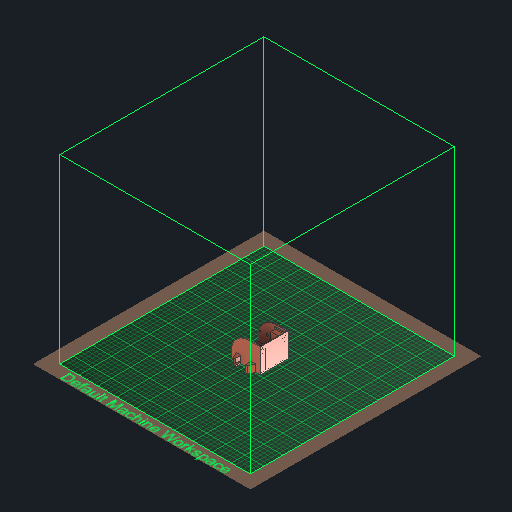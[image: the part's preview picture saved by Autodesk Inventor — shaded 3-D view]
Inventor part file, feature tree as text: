
AUTODESK INVENTOR PART (.ipt)
format: ipt  version: 2022 (Build 260153000, 153)  size: 518,656 bytes
history: native  units: in
note: dims shown in document units (in); Inventor stores cm internally (conversion verified against a paired STEP export)
features: extrude x9, sketch x8, projected_geometry x7, chamfer x3, reference x3, other x3, fillet x1
ambient origin geometry x8: Origin, YZ Plane, XZ Plane, XY Plane, X Axis, Y Axis, Z Axis, Center Point
bodies: Solid1 (feature_tree)
feature tree (34):
  extrude  "Extrusion1"  Depth=2.25in
  extrude  "Extrusion2"  TaperAngle=0.0deg  [1 undecoded]
  fillet  "Fillet1"  Radius=0.05in
  extrude  "Extrusion3"  Depth=0.1in
  extrude  "Extrusion4"  Depth=2.5in TaperAngle=0.0deg
  extrude  "Extrusion5"  Depth=0.1in
  extrude  "Extrusion6"  Depth=0.1in
  chamfer  "Chamfer3"  Distance=0.1in
  chamfer  "Chamfer4"  Distance=0.1in
  extrude  "Extrusion7"  Depth=0.1in
  extrude  "Extrusion8"  Depth=0.25in
  chamfer  "Chamfer5"  Distance=0.1in
  extrude  "Extrusion9"  Depth=1.0in TaperAngle=0.0deg
  sketch  "Sketch1"  dims[d0=2.0in d1=2.25in]
  sketch  "Sketch2"  dims[d2=0.8in d3=0.0in d4=0.05in d5=0.0in]
  projected_geometry  "Projected Loop1"
  projected_geometry  "Projected Loop2"
  projected_geometry  "Projected Loop3"
  projected_geometry  "Projected Loop4"
  sketch  "Sketch4"  dims[d6=0.1in d7=0.1in]
  reference  "Reference1"
  reference  "Reference2"
  reference  "Reference3"
  sketch  "Sketch5"  dims[d8=0.1in d9=2.5in d10=0.0in]
  projected_geometry  "Projected Loop5"
  sketch  "Sketch6"  dims[d11=1.5in d12=0.1in]
  sketch  "Sketch8"  dims[d13=0.1in d14=0.1in]
  sketch  "Sketch9"  dims[d15=0.25in]
  projected_geometry  "Projected Loop6"
  sketch  "Sketch10"  dims[d16=0.1in d17=0.1in d18=0.1in d19=0.1in d20=0.25in d21=0.1in d22=1.0in d23=0.0in d26=0.5in d27=0.0in d28=2.25in d30=0.25in d31=0.1in d32=0.0in d33=0.0in d34=0.0in d38=0.2in d39=0.1in d40=0.0in d41=0.95in d42=1.75in d46=0.5in d47=0.125in d48=0.1718in d49=0.5in d50=0.125in d51=0.1718in d52=0.1111in d53=0.25in d54=0.5in d55=0.0in d56=0.25in d57=0.25in d58=0.25in d59=0.16in d60=0.125in d61=0.125in d62=1.0in d63=0.0in d64=0.25in d65=0.125in d66=45.0deg d67=0.285in d68=45.0deg d69=0.1in d70=0.0in d29=0.0344in]
  projected_geometry  "Projected Loop7"
  parser-record x1  (decoder bookkeeping rows leaked as tree rows — omitted from the tree; the rows remain in map.json)
  other  "Prototype Assembly.iam"
  other  "ServoMotor:1"
note: 1 required parameter value undecoded (feature->parameter linkage not recoverable at this tier; creation-order binding heuristic only, values carry confidence <= 0.55)
note: 1 file-system path scrubbed to <path> (originals preserved in map.json)
